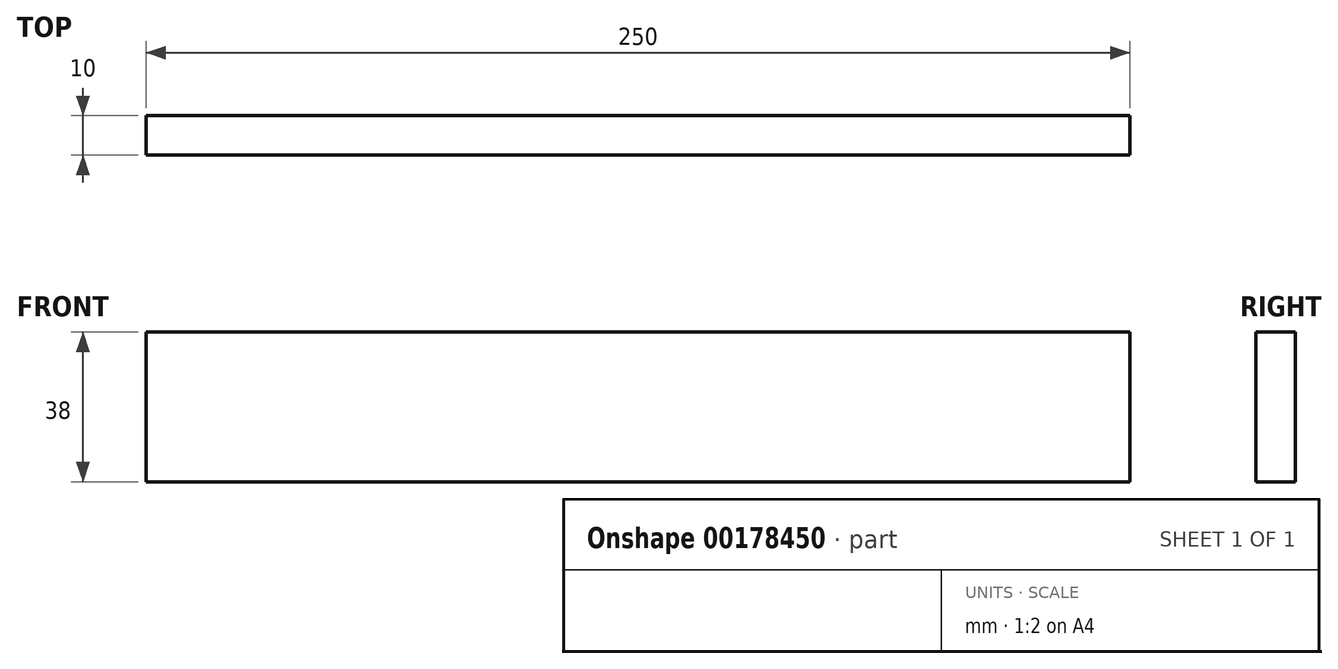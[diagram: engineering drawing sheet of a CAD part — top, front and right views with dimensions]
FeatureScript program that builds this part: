
annotation { "Feature Type Name" : "Feature", "Feature Type Description" : "" }
export const myFeature = defineFeature(function(context is Context, id is Id, definition is map)
    precondition{}
    {
        {
            var Q0;
            Q0=qCreatedBy(makeId("Front.planeOp"),FACE);
            var sketch = newSketch(context, id + "F0", { "sketchPlane" : qUnion([Q0])});
            skLineSegment(sketch, "E0.bottom", {"start": v(0, 0) * mm, "end": v(250, 0) * mm});
            skLineSegment(sketch, "E0.top", {"start": v(0, 38) * mm, "end": v(250, 38) * mm});
            skLineSegment(sketch, "E0.left", {"start": v(0, 0) * mm, "end": v(0, 38) * mm});
            skLineSegment(sketch, "E0.right", {"start": v(250, 0) * mm, "end": v(250, 38) * mm});
            skSolve(sketch);
        }
        {
            var Q0;
            Q0=qSketchRegion(id+"F0",true);
            extrude(context, id + "F1", {"entities" : qUnion([Q0]), "depth" : 10 * mm});
        }
    });
